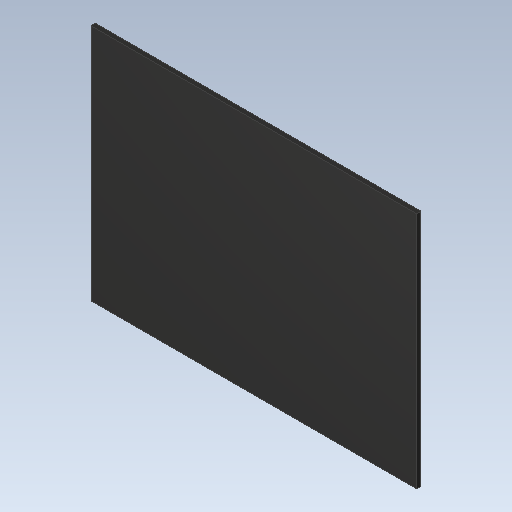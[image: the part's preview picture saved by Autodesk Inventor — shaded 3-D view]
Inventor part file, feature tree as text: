
AUTODESK INVENTOR PART (.ipt)
format: ipt  version: 2023 (Build 270158000, 158)  size: 91,136 bytes
history: imported  units: in
note: dims shown in document units (in); Inventor stores cm internally (conversion verified against a paired STEP export)
features: imported_body x1
ambient origin geometry x8: Origin, YZ Plane, XZ Plane, XY Plane, X Axis, Y Axis, Z Axis, Center Point
bodies: Solid1 (imported_parasolid), Body1 (imported_parasolid)
feature tree (1):
  imported_body  NMx_Import_Brep_tag  [imported B-rep: ~6 faces, bbox_mm=[7.45, 5.45, 0.1]]
